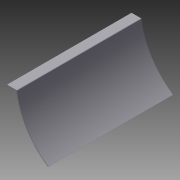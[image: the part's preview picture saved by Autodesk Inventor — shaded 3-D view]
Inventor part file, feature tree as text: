
AUTODESK INVENTOR PART (.ipt)
format: ipt  version: 2012 (Build 160160000, 160)  size: 82,944 bytes
history: native  units: in
note: dims shown in document units (in); Inventor stores cm internally (conversion verified against a paired STEP export)
features: extrude x1, fillet x1, sketch x1
ambient origin geometry x8: Origin, YZ Plane, XZ Plane, XY Plane, X Axis, Y Axis, Z Axis, Center Point
bodies: Solid1 (feature_tree)
feature tree (3):
  extrude  "Extrusion1"  Depth=0.875in
  fillet  "Fillet1"  Radius=6.886in
  sketch  "Sketch1"  dims[d0=0.0625in d1=0.875in d2=6.886in d3=1.0in d4=3.0in d5=0.0625in d6=11.75in d7=0.0in d8=0.0625in]
